# Revit family: Legrand_Three-phase_transformer_with_reduced_losses
name_source: partatom
category: Installations électriques
revit_build: Autodesk Revit 2018 (Build: 20170223_1515(x64)
units: mm (PartAtom-declared; Revit-internal decimal feet)

## family parameters
Basée sur le plan de construction = Non
Conserver l'orientation des annotations = Non
Cote de connecteur circulaire = Utiliser le diamètre
Couper avec des vides une fois chargée = Non
Numéro OmniClass = 23.80.00.00
Partagée = Non
Point de calcul de pièce = Non
Titre OmniClass = Electric Power and Lighting
Toujours verticalement = Oui
Type d'élément = Normal

## types (5) — shared parameters
Fabricant = Legrand
General Conditions of Use = https://export.legrand.com
Modèle = Three-phase isolation transformers
Primary voltage = 400 V en Δ
Secondary voltage = 400 V en Y +N
URL = www.legrand.com

## per-type parameters (varying)
| type | 142860 | 142861 | 142862, 142863 | 142864 | Primary Cable Section | Secondary cable section | Ucc (%) | dimension A | dimension B | dimension C | empty loss | fixing F | fixing G | fixing diameter | max totaly loss | power | weight |
| Three-phase transformer with reduced losses 142860 | Oui | Non | Non | Non | 35 mm² | 35 mm² | 3.5 | 530 mm  [stored 1.73885 ft] | 560 mm  [stored 1.83727 ft] | 460 mm  [stored 1.50919 ft] | 213 W | 320 mm  [stored 1.04987 ft] | 430 mm  [stored 1.41076 ft] | 12 mm  [stored 0.0393701 ft] | 1413 W | 50 kVA | 243.00 kg |
| Three-phase transformer with reduced losses 142861 | Non | Oui | Non | Non | 35 mm² | 35 mm² | 3.0 | 530 mm  [stored 1.73885 ft] | 560 mm  [stored 1.83727 ft] | 540 mm  [stored 1.77165 ft] | 268 W | 320 mm  [stored 1.04987 ft] | 510 mm  [stored 1.67323 ft] | 12 mm  [stored 0.0393701 ft] | 1598 W | 63 kVA | 287.00 kg |
| Three-phase transformer with reduced losses 142862 | Non | Non | Oui | Non | 70 mm² | 70 mm² | 3.2 | 670 mm  [stored 2.19816 ft] | 700 mm  [stored 2.29659 ft] | 610 mm  [stored 2.00131 ft] | 361 W | 400 mm  [stored 1.31234 ft] | 580 mm  [stored 1.90289 ft] | 16 mm  [stored 0.0524934 ft] | 2035 W | 80 kVA | 363.00 kg |
| Three-phase transformer with reduced losses 142863 | Non | Non | Oui | Non | 120 mm² | 70 mm² | 3.0 | 670 mm  [stored 2.19816 ft] | 700 mm  [stored 2.29659 ft] | 610 mm  [stored 2.00131 ft] | 424 W | 400 mm  [stored 1.31234 ft] | 580 mm  [stored 1.90289 ft] | 16 mm  [stored 0.0524934 ft] | 2437 W | 100 kVA | 417.00 kg |
| Three-phase transformer with reduced losses 142864 | Non | Non | Non | Oui | 120 mm² | 120 mm² | 3.1 | 820 mm  [stored 2.69029 ft] | 940 mm  [stored 3.08399 ft] | 880 mm  [stored 2.88714 ft] | 518 W | 500 mm  [stored 1.64042 ft] | 820 mm  [stored 2.69029 ft] | 16 mm  [stored 0.0524934 ft] | 3229 W | 125 kVA | 551.00 kg |

note: [stored X ft] marks values corroborated as IEEE doubles in the binary element streams (Revit-internal decimal feet)
